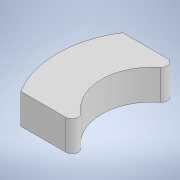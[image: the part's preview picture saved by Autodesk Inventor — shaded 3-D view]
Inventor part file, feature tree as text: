
AUTODESK INVENTOR PART (.ipt)
format: ipt  version: 2022.2 (Build 262287000, 287)  size: 108,032 bytes
history: native  units: mm
features: other x1, extrude x1, fillet x1, sketch x1
ambient origin geometry x8: Origin, YZ Plane, XZ Plane, XY Plane, X Axis, Y Axis, Z Axis, Center Point
bodies: Solid1 (feature_tree)
feature tree (4):
  other  "Crank.ipt"
  extrude  "Extrusion1"  Depth=10.0mm
  fillet  "Fillet1"  Radius=15.0mm
  sketch  "Sketch1"  dims[d0=8.0mm d1=10.0mm d2=15.0mm d3=4.75mm d4=0.0mm d5=1.0mm]
